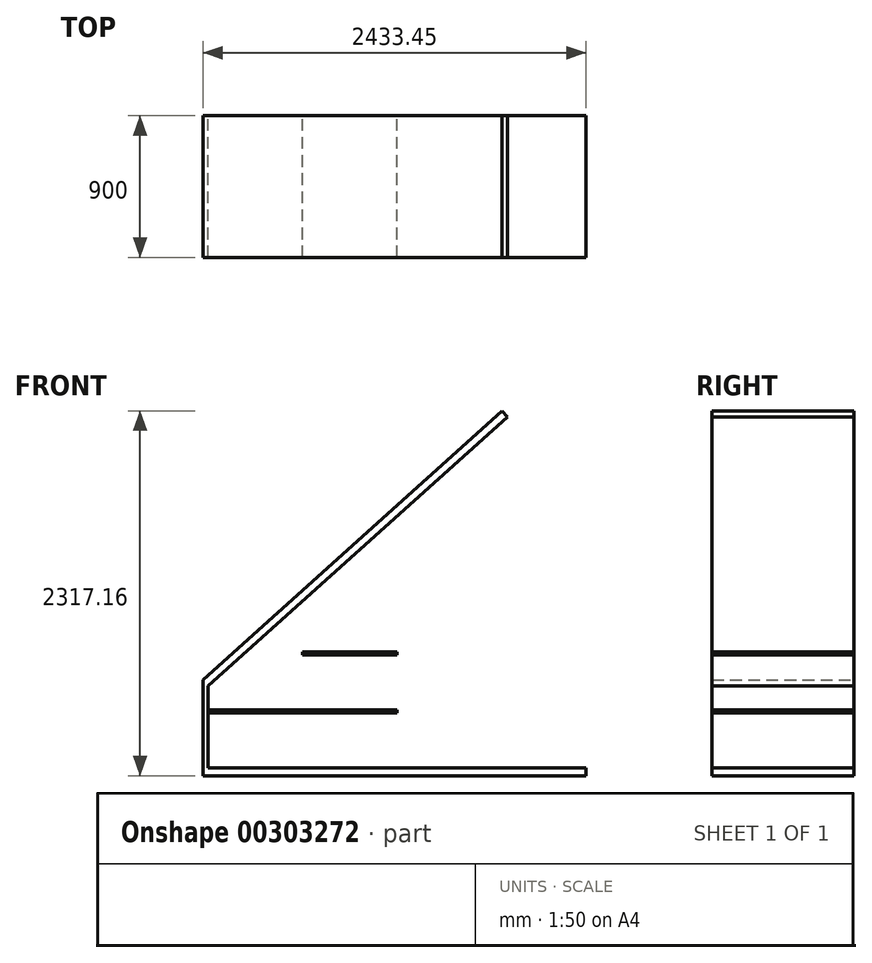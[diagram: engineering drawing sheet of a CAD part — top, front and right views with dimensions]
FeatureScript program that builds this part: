
annotation { "Feature Type Name" : "Feature", "Feature Type Description" : "" }
export const myFeature = defineFeature(function(context is Context, id is Id, definition is map)
    precondition{}
    {
        {
            var Q0;
            Q0=qCreatedBy(makeId("Front.planeOp"),FACE);
            var sketch = newSketch(context, id + "F0", { "sketchPlane" : qUnion([Q0])});
            skLineSegment(sketch, "E0", {"start": v(0, 0) * mm, "end": v(-1900, 0) * mm});
            skLineSegment(sketch, "E1", {"start": v(-1900, 0) * mm, "end": v(-1900, 520) * mm});
            skLineSegment(sketch, "E2", {"start": v(-1900, 520) * mm, "end": v(0, 2230) * mm});
            skLineSegment(sketch, "E3", {"start": v(0, 0) * mm, "end": v(0, 2230) * mm});
            skLineSegment(sketch, "E4.bottom", {"start": v(-1900, 0) * mm, "end": v(500, 0) * mm});
            skLineSegment(sketch, "E4.top", {"start": v(-1900, -50) * mm, "end": v(500, -50) * mm});
            skLineSegment(sketch, "E4.left", {"start": v(-1900, 0) * mm, "end": v(-1900, -50) * mm});
            skLineSegment(sketch, "E4.right", {"start": v(500, 0) * mm, "end": v(500, -50) * mm});
            skLineSegment(sketch, "E5", {"start": v(-1900, 520) * mm, "end": v(-1933.45, 557.16) * mm});
            skLineSegment(sketch, "E6", {"start": v(-1933.45, 557.16) * mm, "end": v(-33.45, 2267.16) * mm});
            skLineSegment(sketch, "E7", {"start": v(-33.45, 2267.16) * mm, "end": v(0, 2230) * mm});
            skLineSegment(sketch, "E8", {"start": v(-1933.45, 557.16) * mm, "end": v(-1933.45, -50) * mm});
            skLineSegment(sketch, "E9", {"start": v(-1933.45, -50) * mm, "end": v(-1900, -50) * mm});
            skLineSegment(sketch, "E10", {"start": v(-33.45, 2267.16) * mm, "end": v(500, 2267.16) * mm});
            skLineSegment(sketch, "E11", {"start": v(500, 2267.16) * mm, "end": v(500, 0) * mm});
            skSolve(sketch);
        }
        {
            var Q0;
            Q0=makeQuery(id+"F0.imprint","IMPRINT",FACE,{"disambiguationData":[TD([[makeQuery(id+"F0.imprint","IMPRINT",EDGE,{"derivedFrom":sQuery(id+"F0.wireOp",EDGE,"E2")}),1.0]])]});
            var Q1;
            Q1=makeQuery(id+"F0.imprint","IMPRINT",FACE,{"disambiguationData":[TD([[makeQuery(id+"F0.imprint","IMPRINT",EDGE,{"derivedFrom":sQuery(id+"F0.wireOp",EDGE,"E1")}),1.0]])]});
            var Q2;
            Q2=makeQuery(id+"F0.imprint","IMPRINT",FACE,{"disambiguationData":[TD([[makeQuery(id+"F0.imprint","IMPRINT",EDGE,{"derivedFrom":sQuery(id+"F0.wireOp",EDGE,"E4.top")}),1.0]])]});
            extrude(context, id + "F1", {"entities" : qUnion([Q0, Q1, Q2]), "depth" : 900 * mm});
        }
        {
            var Q0;
            {var subQ0=sQuery(id+"F0.wireOp",EDGE,"E1");Q0=makeQuery(id+"F0.imprint","IMPRINT",FACE,{"disambiguationData":[TD([[makeQuery(id+"F0.imprint","IMPRINT",EDGE,{"derivedFrom":subQ0}),-1.0]])]});}
            var sketch = newSketch(context, id + "F2", { "sketchPlane" : qUnion([Q0])});
            skLineSegment(sketch, "E12.0", {"start": v(-1900, 0) * mm, "end": v(-1900, 520) * mm});
            skLineSegment(sketch, "E13.0", {"start": v(-1900, 0) * mm, "end": v(500, 0) * mm});
            skLineSegment(sketch, "E14.bottom", {"start": v(-1900, 350) * mm, "end": v(-1300, 350) * mm});
            skLineSegment(sketch, "E14.top", {"start": v(-1900, 368) * mm, "end": v(-1300, 368) * mm});
            skLineSegment(sketch, "E14.left", {"start": v(-1900, 350) * mm, "end": v(-1900, 368) * mm});
            skLineSegment(sketch, "E14.right", {"start": v(-1300, 350) * mm, "end": v(-1300, 368) * mm});
            skLineSegment(sketch, "E15.bottom", {"start": v(-1300, 350) * mm, "end": v(-700, 350) * mm});
            skLineSegment(sketch, "E15.top", {"start": v(-1300, 368) * mm, "end": v(-700, 368) * mm});
            skLineSegment(sketch, "E15.right", {"start": v(-700, 350) * mm, "end": v(-700, 368) * mm});
            skLineSegment(sketch, "E16.bottom", {"start": v(-1300.75, 736) * mm, "end": v(-700.75, 736) * mm});
            skLineSegment(sketch, "E16.top", {"start": v(-1300.75, 718) * mm, "end": v(-700.75, 718) * mm});
            skLineSegment(sketch, "E16.left", {"start": v(-1300.75, 736) * mm, "end": v(-1300.75, 718) * mm});
            skLineSegment(sketch, "E16.right", {"start": v(-700.75, 736) * mm, "end": v(-700.75, 718) * mm});
            skSolve(sketch);
        }
        {
            var Q0;
            Q0=makeQuery(id+"F2.imprint","IMPRINT",FACE,{"disambiguationData":[TD([[makeQuery(id+"F2.imprint","IMPRINT",EDGE,{"derivedFrom":sQuery(id+"F2.wireOp",EDGE,"E14.bottom")}),1.0]])]});
            extrude(context, id + "F3", {"entities" : qUnion([Q0]), "depth" : 900 * mm});
        }
        {
            var Q0;
            Q0=makeQuery(id+"F2.imprint","IMPRINT",FACE,{"disambiguationData":[TD([[makeQuery(id+"F2.imprint","IMPRINT",EDGE,{"derivedFrom":sQuery(id+"F2.wireOp",EDGE,"E15.bottom")}),1.0]])]});
            extrude(context, id + "F4", {"entities" : qUnion([Q0]), "depth" : 900 * mm});
        }
        {
            var Q0;
            Q0=makeQuery(id+"F2.imprint","IMPRINT",FACE,{"disambiguationData":[TD([[makeQuery(id+"F2.imprint","IMPRINT",EDGE,{"derivedFrom":sQuery(id+"F2.wireOp",EDGE,"E16.bottom")}),-1.0]])]});
            extrude(context, id + "F5", {"entities" : qUnion([Q0]), "operationType" : NewBodyOperationType.ADD, "depth" : 900 * mm});
        }
    });
